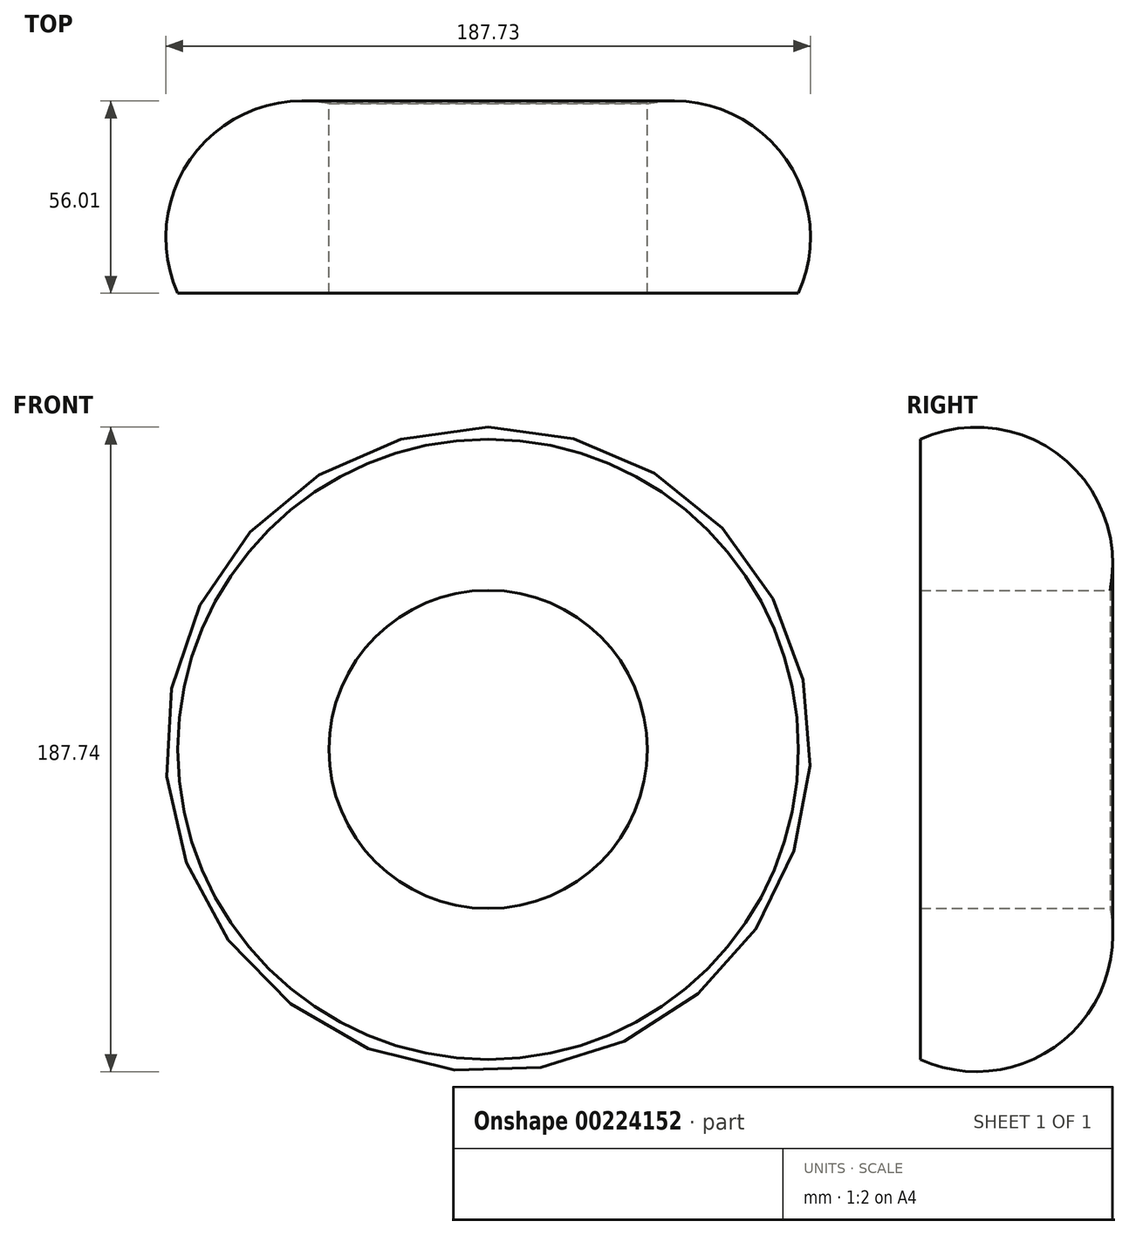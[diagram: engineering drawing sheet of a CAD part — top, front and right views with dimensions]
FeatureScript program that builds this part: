
annotation { "Feature Type Name" : "Feature", "Feature Type Description" : "" }
export const myFeature = defineFeature(function(context is Context, id is Id, definition is map)
    precondition{}
    {
        {
            var Q0;
            Q0=qCreatedBy(makeId("Top.planeOp"),FACE);
            var sketch = newSketch(context, id + "F0", { "sketchPlane" : qUnion([Q0])});
            skArc(sketch, "E0", {"start": v(44.01, 0) * mm, "mid": v(38.87, 41.06) * mm, "end": v(0, 55.23) * mm});
            skLineSegment(sketch, "E1", {"start": v(0, 55.23) * mm, "end": v(0, 0) * mm});
            skLineSegment(sketch, "E2", {"start": v(0, 0) * mm, "end": v(44.01, 0) * mm});
            skLineSegment(sketch, "E3", {"start": v(-46.34, 55.23) * mm, "end": v(-46.34, -31.63) * mm});
            skSolve(sketch);
        }
        {
            var Q0;
            Q0=makeQuery(id+"F0.imprint","IMPRINT",FACE,{"disambiguationData":[TD([[makeQuery(id+"F0.imprint","IMPRINT",EDGE,{"derivedFrom":sQuery(id+"F0.wireOp",EDGE,"E0")}),1.0]])]});
            var Q1;
            Q1=sQuery(id+"F0.wireOp",EDGE,"E3");
            revolve(context, id + "F1", {"entities" : qUnion([Q0]), "axis" : qUnion([Q1]), "revolveType" : RevolveType.FULL});
        }
    });
